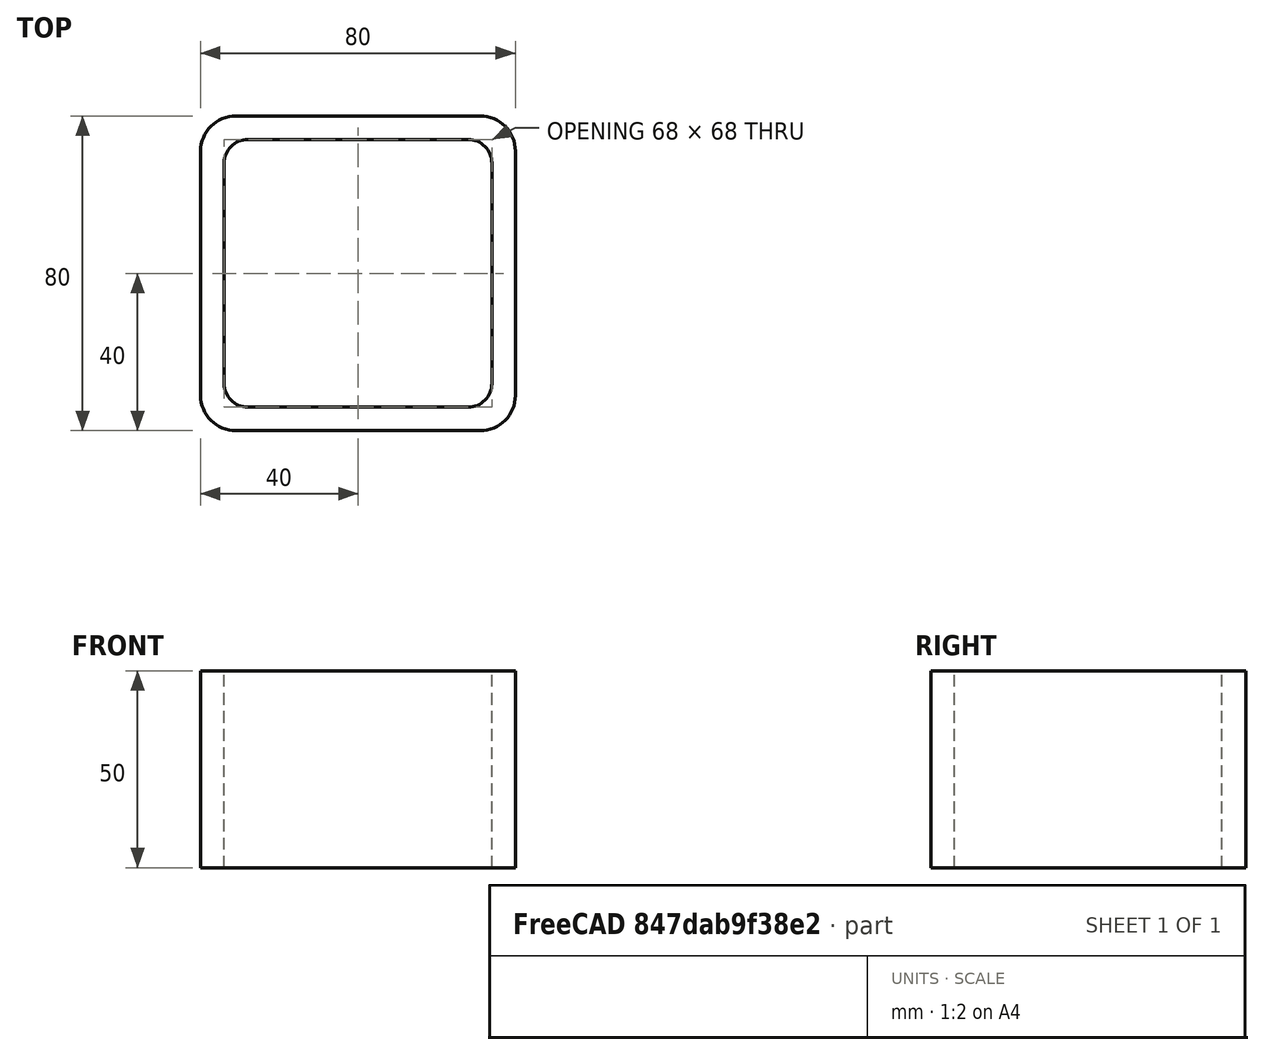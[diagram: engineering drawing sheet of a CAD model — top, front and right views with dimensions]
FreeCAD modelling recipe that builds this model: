
FCSTD DOCUMENT  (FreeCAD 0.15R4671 (Git))
Label: Square hollow section 80x80x6 EN10219 S235JRH
License: All rights reserved
LicenseURL: http://en.wikipedia.org/wiki/All_rights_reserved
objects: Sketcher::SketchObject×1, Part::Extrusion×1
note: 2 computed .brp shape members not serialized (recipe doc carries the construction recipe); baked Part::Feature solids carry a one-line shape summary decoded from their .brp

FEATURE [Sketcher::SketchObject] Sketch
  sketch-geometry (16):
    g0: LineSegment StartX=-28 StartY=34 StartZ=0 EndX=28 EndY=34 EndZ=0
    g1: LineSegment StartX=34 StartY=28 StartZ=0 EndX=34 EndY=-28 EndZ=0
    g2: LineSegment StartX=28 StartY=-34 StartZ=0 EndX=-28 EndY=-34 EndZ=0
    g3: LineSegment StartX=-34 StartY=-28 StartZ=0 EndX=-34 EndY=28 EndZ=0
    g4: LineSegment StartX=-31 StartY=40 StartZ=0 EndX=31 EndY=40 EndZ=0
    g5: LineSegment StartX=40 StartY=31 StartZ=0 EndX=40 EndY=-31 EndZ=0
    g6: LineSegment StartX=31 StartY=-40 StartZ=0 EndX=-31 EndY=-40 EndZ=0
    g7: LineSegment StartX=-40 StartY=-31 StartZ=0 EndX=-40 EndY=31 EndZ=0
    g8: ArcOfCircle CenterX=-28 CenterY=28 CenterZ=0 NormalX=0 NormalY=0 NormalZ=1 Radius=6 StartAngle=1.5708 EndAngle=3.14159
    g9: ArcOfCircle CenterX=28 CenterY=28 CenterZ=0 NormalX=0 NormalY=0 NormalZ=1 Radius=6 StartAngle=0 EndAngle=1.5708
    g10: ArcOfCircle CenterX=28 CenterY=-28 CenterZ=0 NormalX=0 NormalY=0 NormalZ=1 Radius=6 StartAngle=4.71239 EndAngle=6.28319
    g11: ArcOfCircle CenterX=-28 CenterY=-28 CenterZ=0 NormalX=0 NormalY=0 NormalZ=1 Radius=6 StartAngle=3.14159 EndAngle=4.71239
    g12: ArcOfCircle CenterX=31 CenterY=31 CenterZ=0 NormalX=0 NormalY=0 NormalZ=1 Radius=9 StartAngle=0 EndAngle=1.5708
    g13: ArcOfCircle CenterX=31 CenterY=-31 CenterZ=0 NormalX=0 NormalY=0 NormalZ=1 Radius=9 StartAngle=4.71239 EndAngle=6.28319
    g14: ArcOfCircle CenterX=-31 CenterY=-31 CenterZ=0 NormalX=0 NormalY=0 NormalZ=1 Radius=9 StartAngle=3.14159 EndAngle=4.71239
    g15: ArcOfCircle CenterX=-31 CenterY=31 CenterZ=0 NormalX=0 NormalY=0 NormalZ=1 Radius=9 StartAngle=1.5708 EndAngle=3.14159
  constraints (36):
    c: Horizontal(g2)
    c: Vertical(g3)
    c: Horizontal(g6)
    c: Vertical(g7)
    c: Tangent(g3,g8) = 1.5708
    c: Tangent(g0,g8) = 1.5708
    c: Tangent(g0,g9) = 1.5708
    c: Tangent(g1,g9) = 1.5708
    c: Tangent(g1,g10) = 1.5708
    c: Tangent(g2,g10) = 1.5708
    c: Tangent(g2,g11) = 1.5708
    c: Tangent(g3,g11) = 1.5708
    c: Tangent(g4,g12) = 1.5708
    c: Tangent(g5,g12) = 1.5708
    c: Tangent(g5,g13) = 1.5708
    c: Tangent(g6,g13) = 1.5708
    c: Tangent(g6,g14) = 1.5708
    c: Tangent(g7,g14) = 1.5708
    c: Tangent(g7,g15) = 1.5708
    c: Tangent(g4,g15) = 1.5708
    c: Equal(g9,g8)
    c: Equal(g9,g11)
    c: Equal(g9,g10)
    c: Equal(g12,g15)
    c: Equal(g12,g14)
    c: Equal(g12,g13)
    c: Symmetric(g4,g6,g-1)
    c: Symmetric(g7,g5,g-2)
    c: DistanceY(g4,g6) = -80
    c: DistanceX(g7,g5) = 80
    c: Symmetric(g3,g1,g-2)
    c: Symmetric(g0,g2,g-1)
    c: DistanceY(g0,g4) = 6
    c: DistanceX(g5,g1) = -6
    c: Radius(g9) = 6
    c: Radius(g12) = 9
FEATURE [Part::Extrusion] Extrude  label="Square hollow section 80x80x6 EN10219 S235JRH"
  Base = -> Sketch
  Dir = (0,0,50)
  Solid = true
